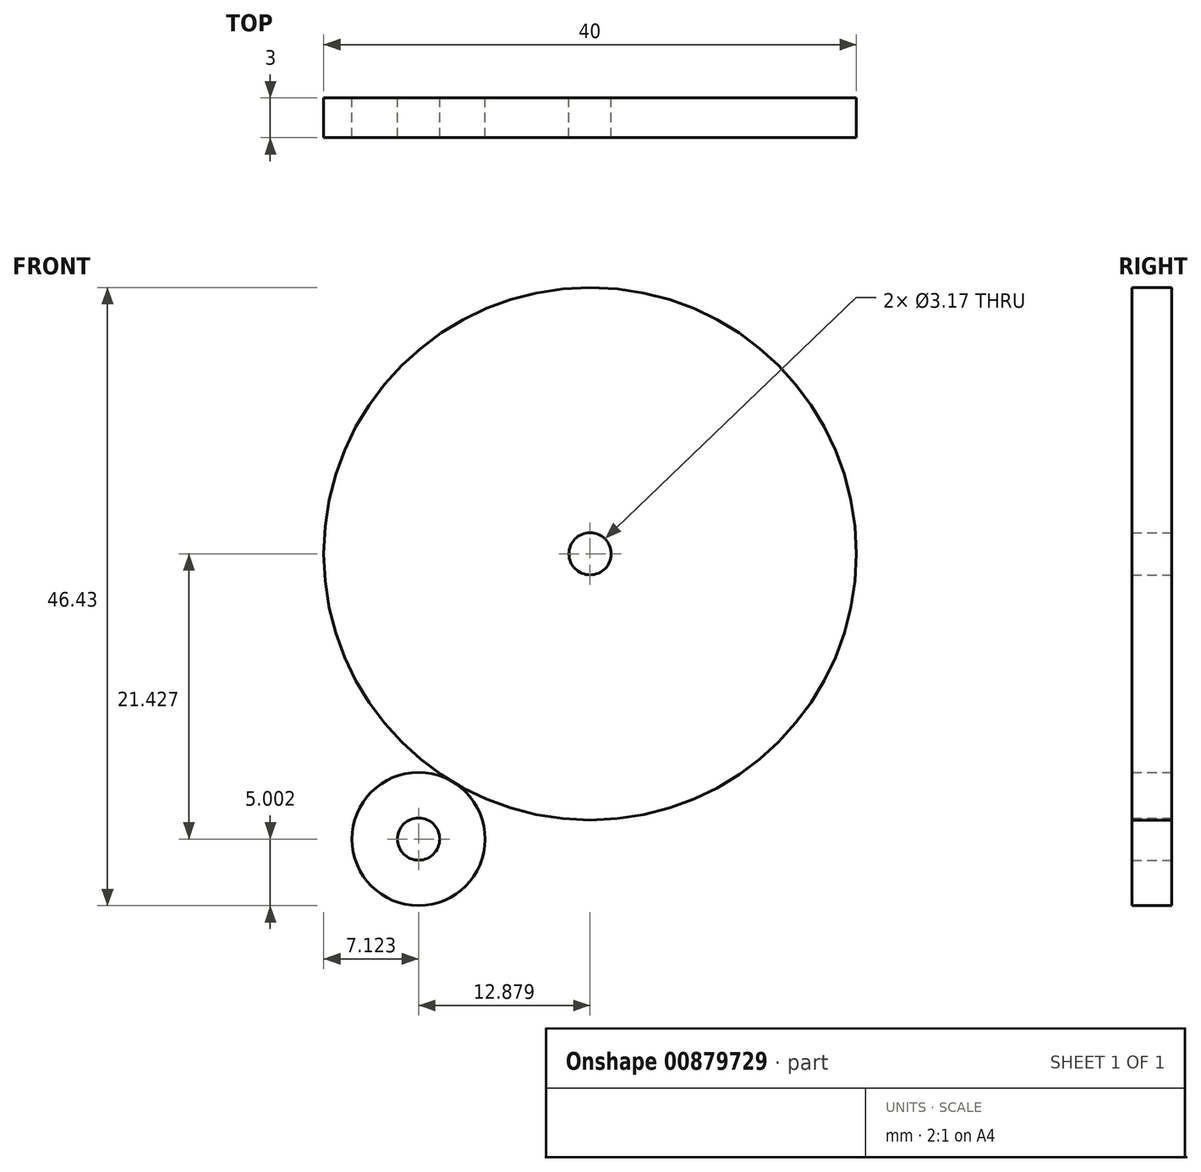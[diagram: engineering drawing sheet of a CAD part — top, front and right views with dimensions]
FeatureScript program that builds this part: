
annotation { "Feature Type Name" : "Feature", "Feature Type Description" : "" }
export const myFeature = defineFeature(function(context is Context, id is Id, definition is map)
    precondition{}
    {
        {
            var Q0;
            Q0=qCreatedBy(makeId("Front.planeOp"),FACE);
            var sketch = newSketch(context, id + "F0", { "sketchPlane" : qUnion([Q0])});
            skCircle(sketch, "E0", {"center": v(-125.97, 31.7) * mm, "radius": 5 * mm});
            skCircle(sketch, "E1", {"center": v(-113.09, 53.13) * mm, "radius": 20 * mm});
            skCircle(sketch, "E2", {"center": v(-113.09, 53.13) * mm, "radius": 1.59 * mm});
            skCircle(sketch, "E3", {"center": v(-125.97, 31.7) * mm, "radius": 1.59 * mm});
            skSolve(sketch);
        }
        {
            var Q0;
            Q0=makeQuery(id+"F0.imprint","IMPRINT",FACE,{"disambiguationData":[TD([[makeQuery(id+"F0.imprint","IMPRINT",EDGE,{"derivedFrom":sQuery(id+"F0.wireOp",EDGE,"E1")}),1.0]])]});
            var Q1;
            Q1=makeQuery(id+"F0.imprint","IMPRINT",FACE,{"disambiguationData":[TD([[makeQuery(id+"F0.imprint","IMPRINT",EDGE,{"derivedFrom":sQuery(id+"F0.wireOp",EDGE,"E0")}),1.0]])]});
            extrude(context, id + "F1", {"entities" : qUnion([Q0, Q1]), "depth" : 3 * mm, "offsetDistance" : 25.4 * mm});
        }
    });
